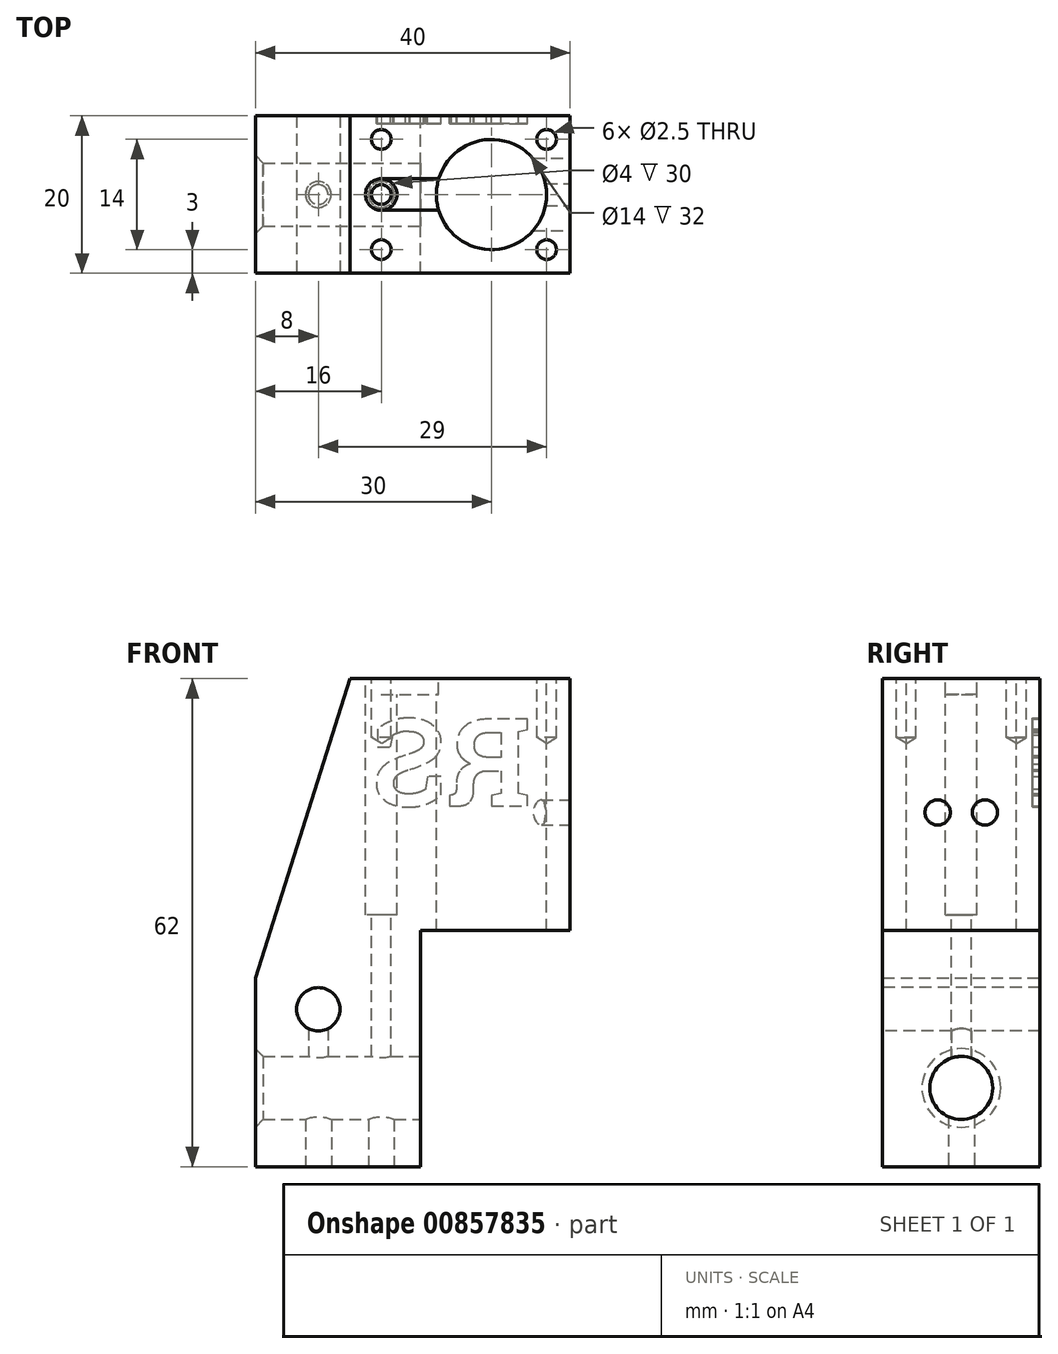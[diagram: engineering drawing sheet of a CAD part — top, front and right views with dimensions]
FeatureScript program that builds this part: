
annotation { "Feature Type Name" : "Feature", "Feature Type Description" : "" }
export const myFeature = defineFeature(function(context is Context, id is Id, definition is map)
    precondition{}
    {
        {
            var Q0;
            Q0=qCreatedBy(makeId("Front.planeOp"),FACE);
            var sketch = newSketch(context, id + "F0", { "sketchPlane" : qUnion([Q0])});
            skLineSegment(sketch, "E0", {"start": v(0, 0) * mm, "end": v(0, 24) * mm});
            skLineSegment(sketch, "E1", {"start": v(0, 0) * mm, "end": v(21, 0) * mm});
            skLineSegment(sketch, "E2", {"start": v(21, 0) * mm, "end": v(21, 30) * mm});
            skLineSegment(sketch, "E3", {"start": v(21, 30) * mm, "end": v(40, 30) * mm});
            skLineSegment(sketch, "E4", {"start": v(40, 30) * mm, "end": v(40, 62) * mm});
            skLineSegment(sketch, "E5", {"start": v(40, 62) * mm, "end": v(12, 62) * mm});
            skLineSegment(sketch, "E6", {"start": v(12, 62) * mm, "end": v(0, 24) * mm});
            skSolve(sketch);
        }
        {
            var Q0;
            Q0=makeQuery(id+"F0.imprint","IMPRINT",FACE,{"disambiguationData":[TD([[makeQuery(id+"F0.imprint","IMPRINT",EDGE,{"derivedFrom":sQuery(id+"F0.wireOp",EDGE,"E0")}),-1.0]])]});
            extrude(context, id + "F1", {"entities" : qUnion([Q0]), "endBound" : BoundingType.SYMMETRIC, "depth" : 20 * mm, "offsetDistance" : 25 * mm});
        }
        {
            var Q0;
            Q0=makeQuery(id+"F1.opExtrude","SWEPT_FACE",FACE,{"disambiguationData":[OSD([sQuery(id+"F0.wireOp",EDGE,"E5")])]});
            var sketch = newSketch(context, id + "F2", { "sketchPlane" : qUnion([Q0])});
            skCircle(sketch, "E7", {"center": v(30, 0) * mm, "radius": 7 * mm});
            skPoint(sketch, "E8", {"position": v(37, 7) * mm});
            skPoint(sketch, "E9", {"position": v(37, -7) * mm});
            skPoint(sketch, "E10", {"position": v(16, 7) * mm});
            skPoint(sketch, "E11", {"position": v(16, -7) * mm});
            skSolve(sketch);
        }
        {
            var Q0;
            Q0=makeQuery(id+"F2.imprint","IMPRINT",FACE,{"disambiguationData":[TD([[makeQuery(id+"F2.imprint","IMPRINT",EDGE,{"derivedFrom":sQuery(id+"F2.wireOp",EDGE,"E7")}),1.0]])]});
            extrude(context, id + "F3", {"entities" : qUnion([Q0]), "operationType" : NewBodyOperationType.REMOVE, "endBound" : BoundingType.THROUGH_ALL, "oppositeDirection" : true, "depth" : 25 * mm, "offsetDistance" : 25 * mm});
        }
        {
            var Q0;
            Q0=sQuery(id+"F2.wireOp",VERTEX,"E10");
            var Q1;
            Q1=sQuery(id+"F2.wireOp",VERTEX,"E11");
            var Q2;
            Q2=sQuery(id+"F2.wireOp",VERTEX,"E9");
            var Q3;
            Q3=sQuery(id+"F2.wireOp",VERTEX,"E8");
            var Q4;
            Q4=makeQuery(id+"F1.opExtrude","SWEPT_BODY",BODY,{"disambiguationData":[OSD([sQuery(id+"F0.wireOp",EDGE,"E0"),sQuery(id+"F0.wireOp",EDGE,"E1"),sQuery(id+"F0.wireOp",EDGE,"E2"),sQuery(id+"F0.wireOp",EDGE,"E3"),sQuery(id+"F0.wireOp",EDGE,"E4"),sQuery(id+"F0.wireOp",EDGE,"E5"),sQuery(id+"F0.wireOp",EDGE,"E6")])]});
            hole(context, id + "F4", {"style" : HoleStyle.SIMPLE, "endStyle" : HoleEndStyle.BLIND, "standardTappedOrClearance" : lookupTablePath({ "standard" : "ISO", "engagement" : "75%", "pitch" : "0.5 mm", "size" : "M3", "type" : "Tapped" }), "standardBlindInLast" : lookupTablePath({ "standard" : "ISO", "engagement" : "75%", "pitch" : "0.5 mm", "size" : "M3", "type" : "Tapped" }), "holeDiameter" : 2.5 * mm, "majorDiameter" : 3 * mm, "showTappedDepth" : true, "holeDepth" : 7.5 * mm, "isTappedThrough" : true, "tappedDepth" : 6 * mm, "tapClearance" : 3, "locations" : qUnion([Q0, Q1, Q2, Q3]), "scope" : qUnion([Q4])});
        }
        {
            var Q0;
            Q0=makeQuery(id+"F2.imprint","IMPRINT",FACE,{"disambiguationData":[TD([[makeQuery(id+"F2.imprint","IMPRINT",EDGE,{"derivedFrom":sQuery(id+"F2.wireOp",EDGE,"E7")}),-1.0]])]});
            var sketch = newSketch(context, id + "F5", { "sketchPlane" : qUnion([Q0])});
            skCircle(sketch, "E12", {"center": v(16, 0) * mm, "radius": 2 * mm});
            skSolve(sketch);
        }
        {
            var Q0;
            Q0=sQuery(id+"F5.wireOp",VERTEX,"E12.center");
            var Q1;
            Q1=makeQuery(id+"F1.opExtrude","SWEPT_BODY",BODY,{"disambiguationData":[OSD([sQuery(id+"F0.wireOp",EDGE,"E0"),sQuery(id+"F0.wireOp",EDGE,"E1"),sQuery(id+"F0.wireOp",EDGE,"E2"),sQuery(id+"F0.wireOp",EDGE,"E3"),sQuery(id+"F0.wireOp",EDGE,"E4"),sQuery(id+"F0.wireOp",EDGE,"E5"),sQuery(id+"F0.wireOp",EDGE,"E6")])]});
            hole(context, id + "F6", {"style" : HoleStyle.C_BORE, "endStyle" : HoleEndStyle.THROUGH, "holeDiameter" : 2.5 * mm, "cBoreDiameter" : 4 * mm, "cBoreDepth" : 30 * mm, "majorDiameter" : 3 * mm, "isTappedThrough" : true, "tappedDepth" : 6 * mm, "tapClearance" : 3, "locations" : qUnion([Q0]), "scope" : qUnion([Q1])});
        }
        {
            var Q0;
            Q0=makeQuery(id+"F2.imprint","IMPRINT",FACE,{"disambiguationData":[TD([[makeQuery(id+"F2.imprint","IMPRINT",EDGE,{"derivedFrom":sQuery(id+"F2.wireOp",EDGE,"E7")}),-1.0]])]});
            var sketch = newSketch(context, id + "F7", { "sketchPlane" : qUnion([Q0])});
            skArc(sketch, "E13", {"start": v(16, -2) * mm, "mid": v(18, 0) * mm, "end": v(16, 2) * mm});
            skLineSegment(sketch, "E14", {"start": v(16, 2) * mm, "end": v(23.3, 2) * mm});
            skLineSegment(sketch, "E15", {"start": v(16, -2) * mm, "end": v(23.32, -2) * mm});
            skArc(sketch, "E16", {"start": v(23.3, 2) * mm, "mid": v(23.06, 0) * mm, "end": v(23.32, -2) * mm});
            skSolve(sketch);
        }
        {
            var Q0;
            {var subQ0=sQuery(id+"F7.wireOp",EDGE,"E13");Q0=makeQuery(id+"F7.imprint","IMPRINT",FACE,{"disambiguationData":[TD([[makeQuery(id+"F7.imprint","IMPRINT",EDGE,{"derivedFrom":subQ0}),-1.0]])]});}
            extrude(context, id + "F8", {"entities" : qUnion([Q0]), "operationType" : NewBodyOperationType.REMOVE, "oppositeDirection" : true, "depth" : 2 * mm, "offsetDistance" : 25 * mm});
        }
        {
            var Q0;
            Q0=makeQuery(id+"F1.opExtrude","SWEPT_FACE",FACE,{"disambiguationData":[OSD([sQuery(id+"F0.wireOp",EDGE,"E4")])]});
            var sketch = newSketch(context, id + "F9", { "sketchPlane" : qUnion([Q0])});
            skCircle(sketch, "E17", {"center": v(-3, 45) * mm, "radius": 1.6 * mm});
            skCircle(sketch, "E18", {"center": v(3, 45) * mm, "radius": 1.6 * mm});
            skCircle(sketch, "E19", {"center": v(0, 10) * mm, "radius": 4 * mm});
            skSolve(sketch);
        }
        {
            var Q0;
            Q0=makeQuery(id+"F9.imprint","IMPRINT",FACE,{"disambiguationData":[TD([[makeQuery(id+"F9.imprint","IMPRINT",EDGE,{"derivedFrom":sQuery(id+"F9.wireOp",EDGE,"E19")}),1.0]])]});
            extrude(context, id + "F10", {"entities" : qUnion([Q0]), "operationType" : NewBodyOperationType.REMOVE, "endBound" : BoundingType.THROUGH_ALL, "oppositeDirection" : true, "depth" : 25 * mm, "offsetDistance" : 25 * mm});
        }
        {
            var Q0;
            Q0 = qSketchRegion(id + "F9", true);
            extrude(context, id + "F11", {"entities" : qUnion([Q0]), "operationType" : NewBodyOperationType.REMOVE, "oppositeDirection" : true, "depth" : 10 * mm, "offsetDistance" : 25 * mm});
        }
        {
            var Q0;
            Q0=makeQuery(id+"F10.boolean.opBoolean","INTERSECT",EDGE,{"derivedFrom":[makeQuery(id+"F1.opExtrude","SWEPT_FACE",FACE,{"disambiguationData":[OSD([sQuery(id+"F0.wireOp",EDGE,"E0")])]}),makeQuery(id+"F10.opExtrude","SWEPT_FACE",FACE,{"disambiguationData":[OSD([sQuery(id+"F9.wireOp",EDGE,"E19")])]})]});
            chamfer(context, id + "F12", {"entities" : qUnion([Q0]), "width" : 1 * mm, "tangentPropagation" : true});
        }
        {
            var Q0;
            Q0=makeQuery(id+"F1.opExtrude","CAP_FACE",FACE,{"disambiguationData":[OSD([sQuery(id+"F0.wireOp",EDGE,"E0"),sQuery(id+"F0.wireOp",EDGE,"E1"),sQuery(id+"F0.wireOp",EDGE,"E2"),sQuery(id+"F0.wireOp",EDGE,"E3"),sQuery(id+"F0.wireOp",EDGE,"E4"),sQuery(id+"F0.wireOp",EDGE,"E5"),sQuery(id+"F0.wireOp",EDGE,"E6")])],"isStart":false});
            var sketch = newSketch(context, id + "F13", { "sketchPlane" : qUnion([Q0])});
            skPoint(sketch, "E20", {"position": v(8, 20) * mm});
            skSolve(sketch);
        }
        {
            var Q0;
            Q0=sQuery(id+"F13.wireOp",VERTEX,"E20");
            var Q1;
            Q1=makeQuery(id+"F1.opExtrude","SWEPT_BODY",BODY,{"disambiguationData":[OSD([sQuery(id+"F0.wireOp",EDGE,"E0"),sQuery(id+"F0.wireOp",EDGE,"E1"),sQuery(id+"F0.wireOp",EDGE,"E2"),sQuery(id+"F0.wireOp",EDGE,"E3"),sQuery(id+"F0.wireOp",EDGE,"E4"),sQuery(id+"F0.wireOp",EDGE,"E5"),sQuery(id+"F0.wireOp",EDGE,"E6")])]});
            hole(context, id + "F14", {"style" : HoleStyle.SIMPLE, "endStyle" : HoleEndStyle.THROUGH, "standardTappedOrClearance" : lookupTablePath({ "fit" : "Normal", "standard" : "ISO", "size" : "M5", "type" : "Clearance" }), "standardBlindInLast" : lookupTablePath({ "fit" : "Standard", "standard" : "ISO", "size" : "M5", "type" : "Clearance" }), "holeDiameter" : 5.5 * mm, "majorDiameter" : 5 * mm, "isTappedThrough" : true, "tappedDepth" : 6 * mm, "tapClearance" : 3, "locations" : qUnion([Q0]), "scope" : qUnion([Q1])});
        }
        {
            var Q0;
            Q0=makeQuery(id+"F1.opExtrude","SWEPT_FACE",FACE,{"disambiguationData":[OSD([sQuery(id+"F0.wireOp",EDGE,"E1")])]});
            var sketch = newSketch(context, id + "F15", { "sketchPlane" : qUnion([Q0])});
            skPoint(sketch, "E21", {"position": v(8, 0) * mm});
            skPoint(sketch, "E22", {"position": v(16, 0) * mm});
            skSolve(sketch);
        }
        {
            var Q0;
            Q0=sQuery(id+"F15.wireOp",VERTEX,"E21");
            var Q1;
            Q1=sQuery(id+"F15.wireOp",VERTEX,"E22");
            var Q2;
            Q2=makeQuery(id+"F1.opExtrude","SWEPT_BODY",BODY,{"disambiguationData":[OSD([sQuery(id+"F0.wireOp",EDGE,"E0"),sQuery(id+"F0.wireOp",EDGE,"E1"),sQuery(id+"F0.wireOp",EDGE,"E2"),sQuery(id+"F0.wireOp",EDGE,"E3"),sQuery(id+"F0.wireOp",EDGE,"E4"),sQuery(id+"F0.wireOp",EDGE,"E5"),sQuery(id+"F0.wireOp",EDGE,"E6")])]});
            hole(context, id + "F16", {"style" : HoleStyle.SIMPLE, "endStyle" : HoleEndStyle.BLIND, "holeDiameter" : 3.3 * mm, "majorDiameter" : 4 * mm, "holeDepth" : 8.1 * mm, "isTappedThrough" : true, "tappedDepth" : 6 * mm, "tapClearance" : 3, "locations" : qUnion([Q0, Q1]), "scope" : qUnion([Q2])});
        }
        {
            var Q0;
            Q0=makeQuery(id+"F1.opExtrude","SWEPT_FACE",FACE,{"disambiguationData":[OSD([sQuery(id+"F0.wireOp",EDGE,"E1")])]});
            var sketch = newSketch(context, id + "F17", { "sketchPlane" : qUnion([Q0])});
            skCircle(sketch, "E23", {"center": v(8, 0) * mm, "radius": 1.25 * mm});
            skSolve(sketch);
        }
        {
            var Q0;
            Q0=makeQuery(id+"F17.imprint","IMPRINT",FACE,{"disambiguationData":[TD([[makeQuery(id+"F17.imprint","IMPRINT",EDGE,{"derivedFrom":sQuery(id+"F17.wireOp",EDGE,"E23")}),1.0]])]});
            extrude(context, id + "F18", {"entities" : qUnion([Q0]), "operationType" : NewBodyOperationType.REMOVE, "oppositeDirection" : true, "depth" : 20 * mm, "offsetDistance" : 25 * mm});
        }
        {
            var Q0;
            Q0=makeQuery(id+"F1.opExtrude","CAP_FACE",FACE,{"disambiguationData":[OSD([sQuery(id+"F0.wireOp",EDGE,"E0"),sQuery(id+"F0.wireOp",EDGE,"E1"),sQuery(id+"F0.wireOp",EDGE,"E2"),sQuery(id+"F0.wireOp",EDGE,"E3"),sQuery(id+"F0.wireOp",EDGE,"E4"),sQuery(id+"F0.wireOp",EDGE,"E5"),sQuery(id+"F0.wireOp",EDGE,"E6")])],"isStart":true});
            var sketch = newSketch(context, id + "F19", { "sketchPlane" : qUnion([Q0])});
            skText(sketch, "E24", { "text": "RS", "fontName": "RobotoSlab-Bold.ttf"});
            const initialGuessF19  = {"E24": [-0.035, 0.04583, 1, 0, 0.01117]};
            skSetInitialGuess(sketch, initialGuessF19);
            skSolve(sketch);
        }
        {
            var Q0;
            Q0=makeQuery(id+"F19.imprint","IMPRINT",FACE,{"disambiguationData":[TD([[makeQuery(id+"F19.imprint","IMPRINT",EDGE,{"derivedFrom":sQuery(id+"F19.wireOp",EDGE,"E24.sketch_text.stroke-0")}),-1.0]])]});
            var Q1;
            Q1=makeQuery(id+"F19.imprint","IMPRINT",FACE,{"disambiguationData":[TD([[makeQuery(id+"F19.imprint","IMPRINT",EDGE,{"derivedFrom":sQuery(id+"F19.wireOp",EDGE,"E24.sketch_text.stroke-36")}),-1.0]])]});
            extrude(context, id + "F20", {"entities" : qUnion([Q0, Q1]), "operationType" : NewBodyOperationType.REMOVE, "oppositeDirection" : true, "depth" : 1 * mm, "offsetDistance" : 25 * mm});
        }
    });
